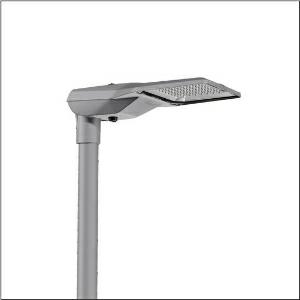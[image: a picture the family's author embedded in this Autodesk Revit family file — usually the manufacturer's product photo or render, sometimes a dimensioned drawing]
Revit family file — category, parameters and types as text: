
# Revit family: streetlight_sl_21_midi___stw1_0a_5xe3e63t08nb_c3f7
name_source: partatom
category: Lighting Fixtures
units: mm (PartAtom-declared; Revit-internal decimal feet)

## family parameters
Cut with Voids When Loaded = No
Host = Face
Light Source = No
Part Type = Normal
Room Calculation Point = No
Round Connector Dimension = Use Diameter
Shared = No

## types (1)
- --- (1 x LED, 20350 lm, 151.2 W, 2700K)
    Apparent Load = 151 VA
    CIE Flux Codes = 39 75 98 100 100
    Color Rendering = 70
    Color Temperature = 2700K
    Default Elevation = 1800 mm
    Description = Streetlight SL 21 midi, mast luminaire, primary light control with lens, of PMMA, primary optical cover: cover, of toughened safety glass, transparent, light distribution: STW1.0a, light emission: direct distribution, primary light characteristic: asymmetric, installation type: side-entry, post-top, LED, High Power LED, rated luminous flux: 20.350lm, luminous efficacy: 135lm/W, light colour: 727, colour temperature: 2700K, control gear: D4i, control: overheat protection, constant luminous flux control, time-dependent luminous flux control, flexible luminous flux parameterisation, pre-setting: logarithmic dimming characteristic, mains connection: 230..240V, AC, 50/60Hz, start of lifetime: 151W, end of service life: 157W, reduction: 70W, luminaire housing, of diecast aluminium, powder-coated, Siteco® metallic grey (DB 702S), corrosivity category C5 mid according to DIN EN ISO 12944, please order mast flange separately, inclination adjustable: 0°, 5°, 10°, 15°, sealing non-destructively replaceable, multi-level sealing system, length: 644mm, width: 335mm, height: 110mm, mast flange for spigot size: 42mm (side-entry): 5XC10008XM4, 60/48mm (side-entry/post-top): 5XC10108XM2, 76/60mm (side-entry/post-top): 5XC10108XM1, mounting height: 4..8m, Smart Interface below and above, protection rating (complete): IP66, insulation class (complete): insulation class II (safety insulation), certification: CE, ENEC, ENEC+, VDE, impact resistance: IK10, permissible operating ambient temperature for outdoor applications: -40..+50°C, standard-compliant lighting for roads and squares, packaging unit: 1 piece

Light Distribution: STW1.0a
    Height = 111 mm
    Lamp = 1 x LED
    Lamp Light Flux = 20350 lm
    Lamp Power = 151.2 W
    Lamp count = 1
    Length = 644 mm
    Luminous efficacy = 135 lm/W
    Manufacturer = Siteco
    ModVariant = No
    Model = 5XE3E63T08NB
    Number of Poles = 1
    OnlyDefault = Yes
    Power Factor = 1
    Product Name = Streetlight SL 21 midi | STW1.0a
    Product group = mast luminaire | pylon top
    ProductGroupID = 6100
    Protection Class = Protection class II
    Protection Degree = IP 66
    RLX_Detail_Level = 1
    RLX_Emergency_Light_Flux = 0 lm
    RLX_Emergency_Type = 0
    RLX_Emergency_Type_DB = No
    RlxData = <blob elided: 27217 chars, md5=abdd59f1>
    Socket = socket
    Standby Power = 0 W
    System Light Flux = 20350 lm
    System Power = 151 W
    Type Comments = factory setting: luminous flux: 100 % | dim-lin: 254 | 802 mA
    Type Image = l_1004304.jpg
    URL = http://relux.com
    VarID = @adj_190961
    Voltage = 0 V
    Weight = 0.00 kg
    Width = 336 mm

## geometry (parser evidence)
native form markers: Blend x4, Sweep x12
no freeform markers — native parametric forms only
